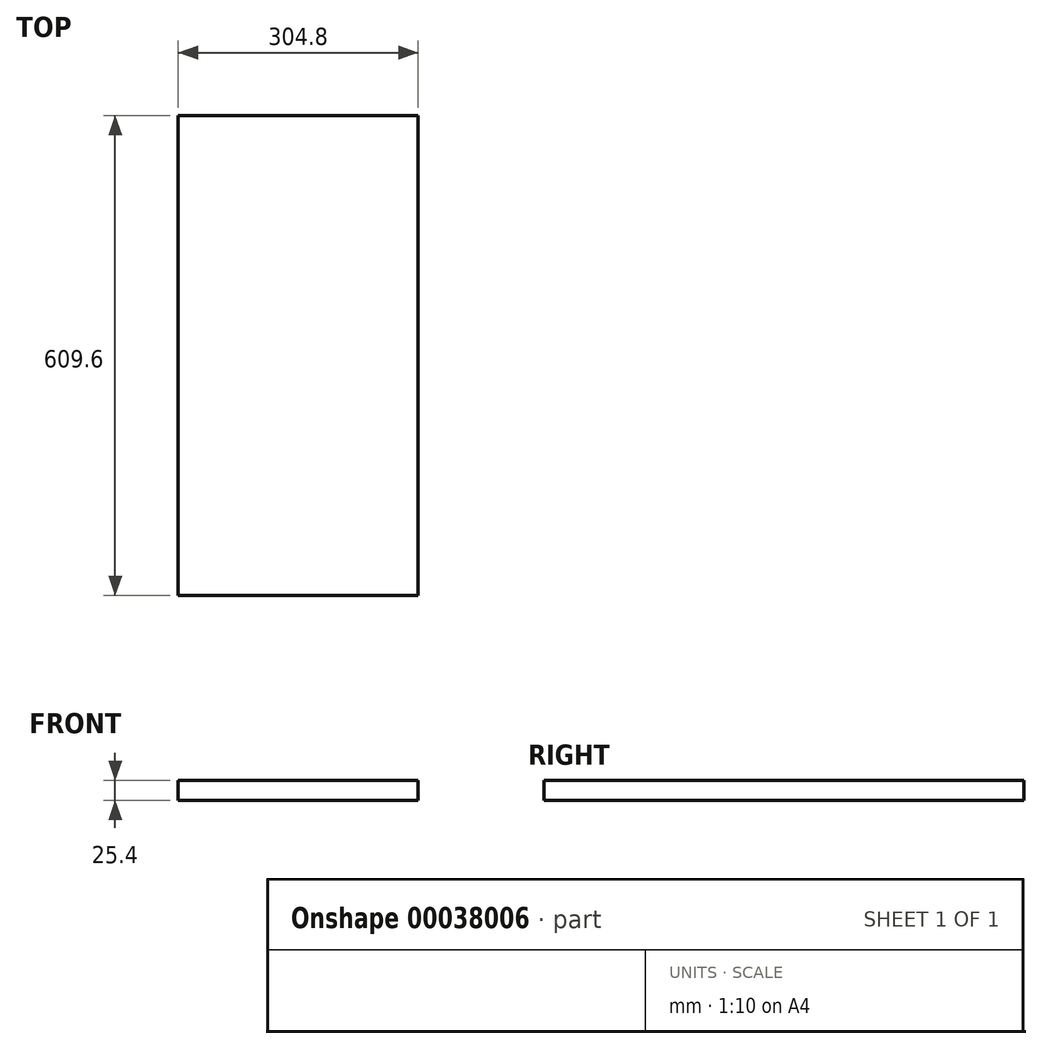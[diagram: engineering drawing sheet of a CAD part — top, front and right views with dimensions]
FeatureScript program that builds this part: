
annotation { "Feature Type Name" : "Feature", "Feature Type Description" : "" }
export const myFeature = defineFeature(function(context is Context, id is Id, definition is map)
    precondition{}
    {
        {
            var Q0;
            Q0=qCreatedBy(makeId("Top.planeOp"),FACE);
            var sketch = newSketch(context, id + "F0", { "sketchPlane" : qUnion([Q0])});
            skLineSegment(sketch, "E0.bottom", {"start": v(0, 0) * mm, "end": v(-304.8, 0) * mm});
            skLineSegment(sketch, "E0.top", {"start": v(0, -609.6) * mm, "end": v(-304.8, -609.6) * mm});
            skLineSegment(sketch, "E0.left", {"start": v(0, 0) * mm, "end": v(0, -609.6) * mm});
            skLineSegment(sketch, "E0.right", {"start": v(-304.8, 0) * mm, "end": v(-304.8, -609.6) * mm});
            skSolve(sketch);
        }
        {
            var Q0;
            Q0 = qSketchRegion(id + "F0", true);
            extrude(context, id + "F1", {"entities" : qUnion([Q0]), "depth" : 25.4 * mm});
        }
    });
